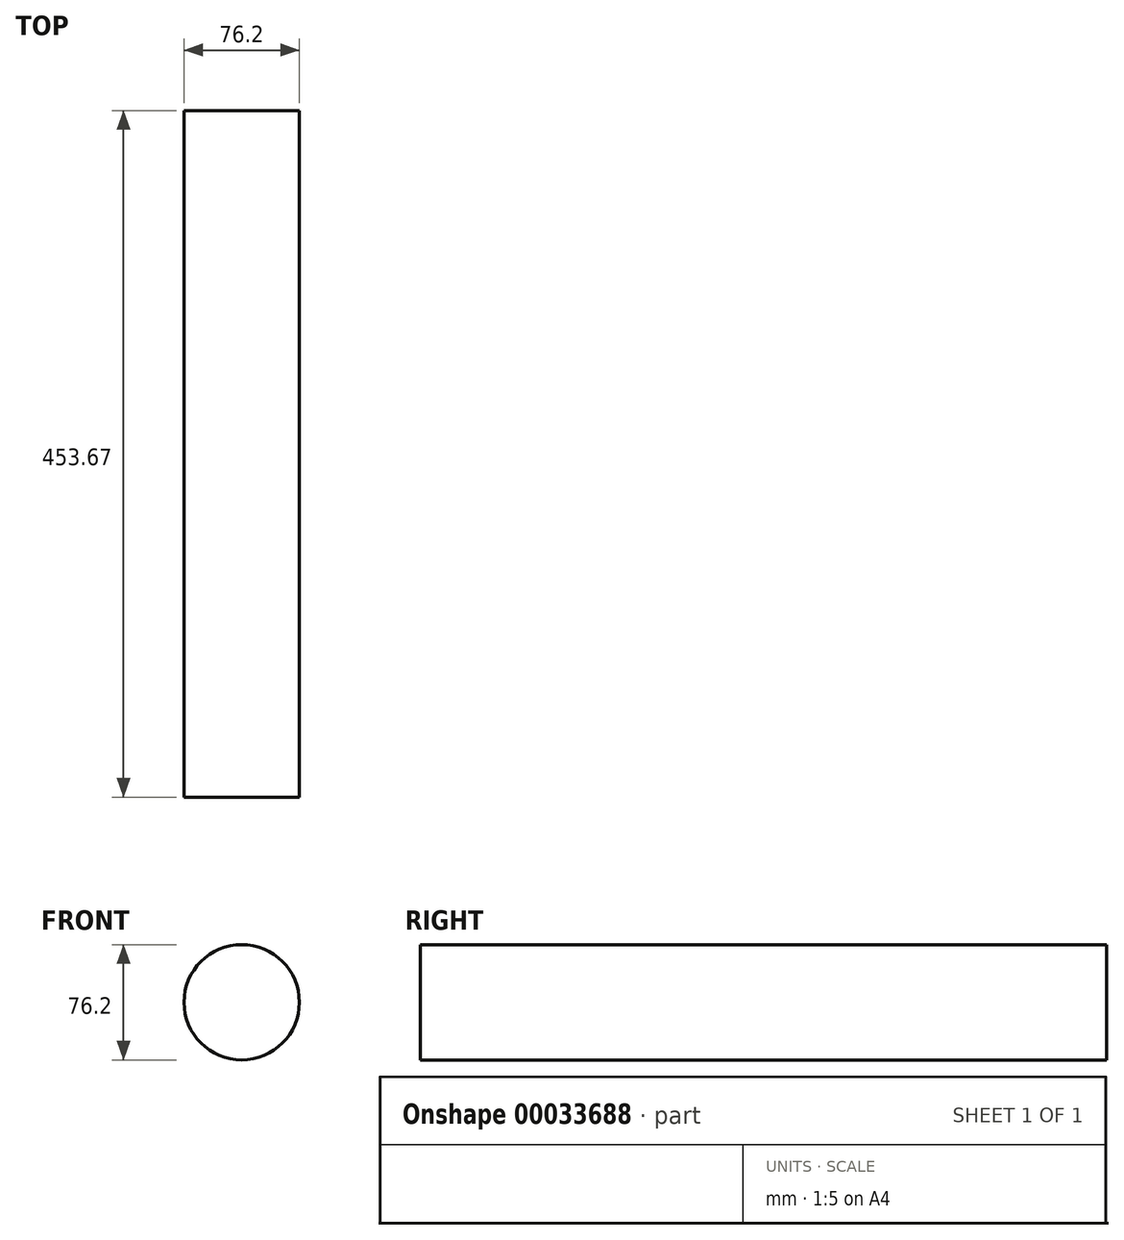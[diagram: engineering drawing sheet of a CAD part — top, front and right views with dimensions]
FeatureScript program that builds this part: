
annotation { "Feature Type Name" : "Feature", "Feature Type Description" : "" }
export const myFeature = defineFeature(function(context is Context, id is Id, definition is map)
    precondition{}
    {
        {
            var Q0;
            Q0=qCreatedBy(makeId("Front.planeOp"),FACE);
            var sketch = newSketch(context, id + "F0", { "sketchPlane" : qUnion([Q0])});
            skCircle(sketch, "E0", {"center": v(0, 0) * mm, "radius": 38.1 * mm});
            skSolve(sketch);
        }
        {
            var Q0;
            Q0 = qSketchRegion(id + "F0", true);
            extrude(context, id + "F1", {"entities" : qUnion([Q0]), "depth" : 453.67 * mm});
        }
    });
